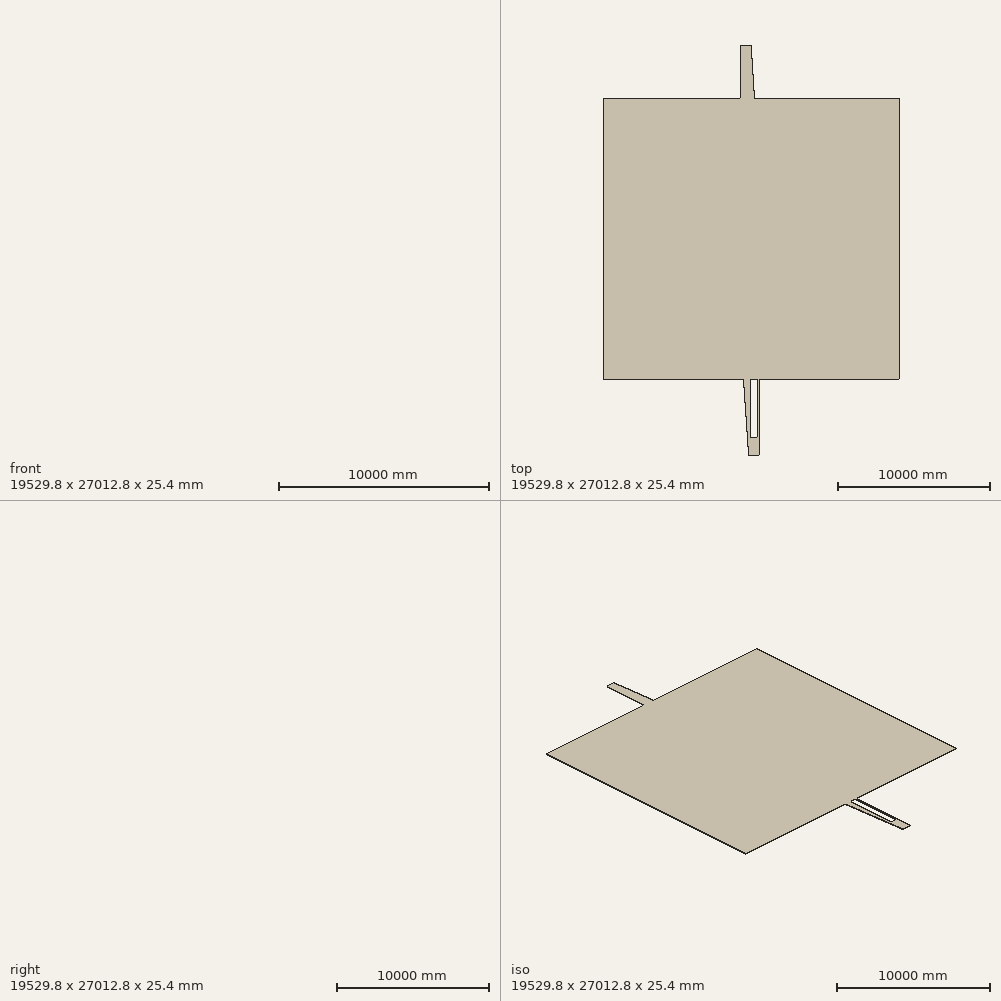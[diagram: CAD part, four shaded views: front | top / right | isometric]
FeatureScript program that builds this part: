
annotation { "Feature Type Name" : "Feature", "Feature Type Description" : "" }
export const myFeature = defineFeature(function(context is Context, id is Id, definition is map)
    precondition{}
    {
        {
            var Q0;
            Q0=qCreatedBy(makeId("Top.planeOp"),FACE);
            var sketch = newSketch(context, id + "F0", { "sketchPlane" : qUnion([Q0])});
            skLineSegment(sketch, "E0.bottom", {"start": v(-309.72, 8391.7) * mm, "end": v(366.98, 8391.7) * mm});
            skLineSegment(sketch, "E0.top", {"start": v(-309.72, -11196.4) * mm, "end": v(366.98, -11196.4) * mm});
            skLineSegment(sketch, "E0.left", {"start": v(-309.72, 8391.7) * mm, "end": v(-309.72, -11196.4) * mm});
            skLineSegment(sketch, "E0.right", {"start": v(366.98, 8391.7) * mm, "end": v(366.98, -11196.4) * mm});
            skLineSegment(sketch, "E1.bottom", {"start": v(789.19, -6286.23) * mm, "end": v(319.66, -6286.23) * mm});
            skLineSegment(sketch, "E1.top", {"start": v(789.19, -17411.82) * mm, "end": v(319.66, -17411.82) * mm});
            skLineSegment(sketch, "E1.left", {"start": v(789.19, -6286.23) * mm, "end": v(789.19, -17411.82) * mm});
            skLineSegment(sketch, "E1.right", {"start": v(319.66, -6286.23) * mm, "end": v(319.66, -17411.82) * mm});
            skLineSegment(sketch, "E2.bottom", {"start": v(200.04, -1647.4) * mm, "end": v(895.83, -1647.4) * mm});
            skLineSegment(sketch, "E2.top", {"start": v(200.04, -18621.08) * mm, "end": v(895.83, -18621.08) * mm});
            skLineSegment(sketch, "E2.left", {"start": v(200.04, -1647.4) * mm, "end": v(200.04, -18621.08) * mm});
            skLineSegment(sketch, "E2.right", {"start": v(895.83, -1647.4) * mm, "end": v(895.83, -18621.08) * mm});
            skLineSegment(sketch, "E3", {"start": v(-183.24, 6365.45) * mm, "end": v(200.04, -1647.4) * mm});
            skLineSegment(sketch, "E4", {"start": v(721.85, -26290.35) * mm, "end": v(-150.1, -14642.01) * mm});
            skLineSegment(sketch, "E5", {"start": v(-150.1, -14642.01) * mm, "end": v(200.04, -18621.08) * mm});
            skLineSegment(sketch, "E6", {"start": v(-309.72, -11196.4) * mm, "end": v(200.04, -18621.08) * mm});
            skLineSegment(sketch, "E7", {"start": v(596.44, -14831.35) * mm, "end": v(200.04, -8589.65) * mm});
            skLineSegment(sketch, "E8", {"start": v(200.04, -8589.65) * mm, "end": v(895.83, 0) * mm});
            skLineSegment(sketch, "E9", {"start": v(895.83, 0) * mm, "end": v(366.98, 8391.7) * mm});
            skLineSegment(sketch, "E10", {"start": v(1279.18, -31676.48) * mm, "end": v(1497.48, -43084.88) * mm});
            skLineSegment(sketch, "E11", {"start": v(1497.48, -43084.88) * mm, "end": v(3934.88, -70677.1) * mm});
            skSolve(sketch);
        }
        {
            var Q0;
            Q0 = qSketchRegion(id + "F0", true);
            extrude(context, id + "F1", {"entities" : qUnion([Q0]), "depth" : 25.4 * mm, "offsetDistance" : 25.4 * mm});
        }
        {
            var Q0;
            Q0=qCreatedBy(makeId("Top.planeOp"),FACE);
            var sketch = newSketch(context, id + "F2", { "sketchPlane" : qUnion([Q0])});
            skLineSegment(sketch, "E12.bottom", {"start": v(-9376.92, -13606.68) * mm, "end": v(10152.84, -13606.68) * mm});
            skLineSegment(sketch, "E12.top", {"start": v(-9376.92, 4921.64) * mm, "end": v(10152.84, 4921.64) * mm});
            skLineSegment(sketch, "E12.left", {"start": v(-9376.92, -13606.68) * mm, "end": v(-9376.92, 4921.64) * mm});
            skLineSegment(sketch, "E12.right", {"start": v(10152.84, -13606.68) * mm, "end": v(10152.84, 4921.64) * mm});
            skSolve(sketch);
        }
        {
            var Q0;
            Q0 = qSketchRegion(id + "F2", true);
            extrude(context, id + "F3", {"entities" : qUnion([Q0]), "operationType" : NewBodyOperationType.ADD, "depth" : 25.4 * mm, "offsetDistance" : 25.4 * mm});
        }
    });
